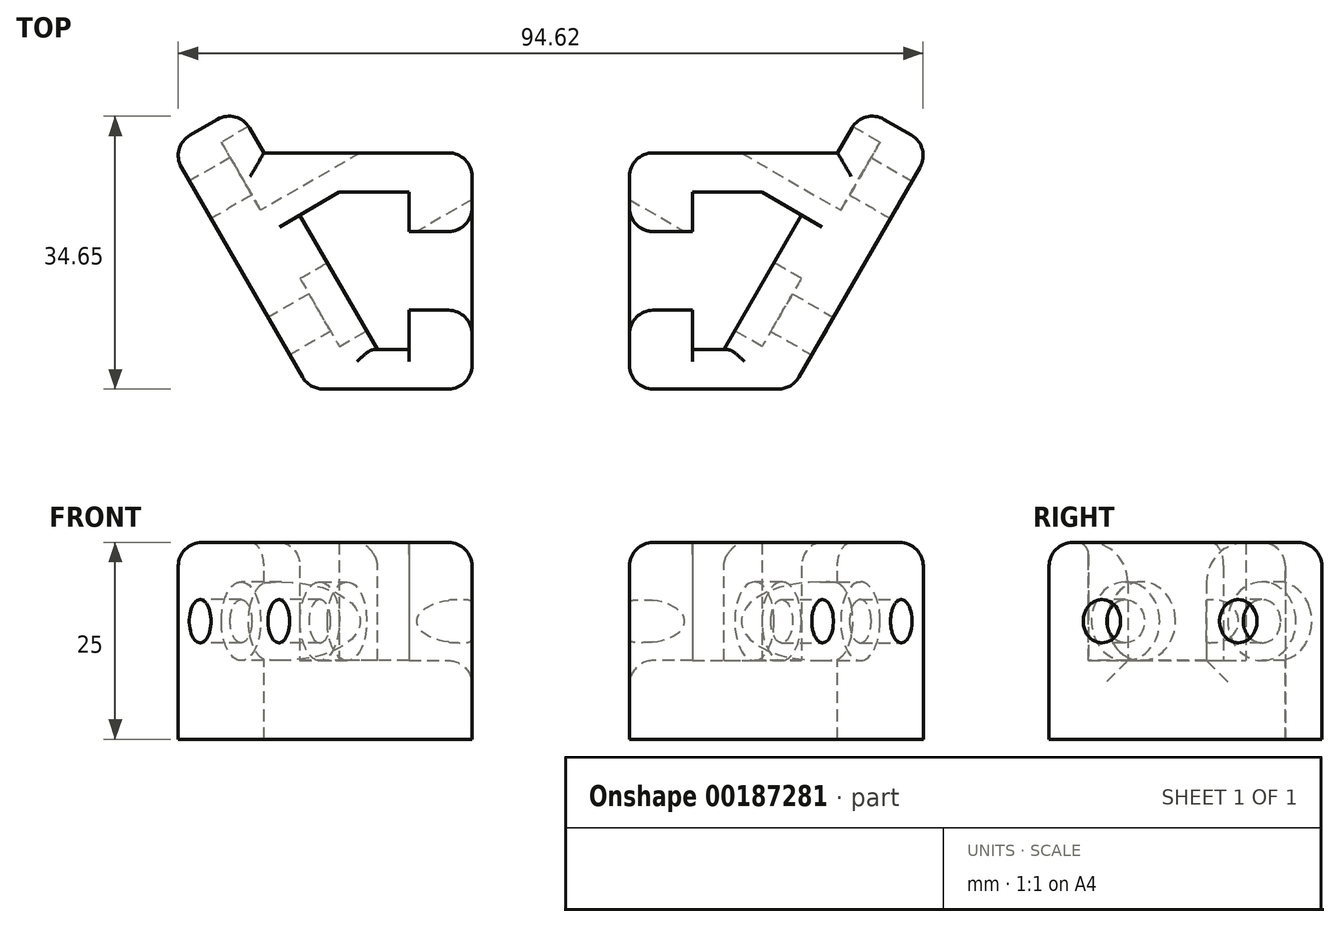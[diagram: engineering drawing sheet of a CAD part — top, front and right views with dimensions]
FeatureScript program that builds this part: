
annotation { "Feature Type Name" : "Feature", "Feature Type Description" : "" }
export const myFeature = defineFeature(function(context is Context, id is Id, definition is map)
    precondition{}
    {
        {
            var Q0;
            Q0=qCreatedBy(makeId("Top.planeOp"),FACE);
            var sketch = newSketch(context, id + "F0", { "sketchPlane" : qUnion([Q0])});
            skLineSegment(sketch, "E0.bottom", {"start": v(-4, 10) * mm, "end": v(4, 10) * mm});
            skLineSegment(sketch, "E0.top", {"start": v(-4, -10) * mm, "end": v(4, -10) * mm});
            skLineSegment(sketch, "E0.left", {"start": v(-4, 10) * mm, "end": v(-4, -10) * mm});
            skLineSegment(sketch, "E0.right", {"start": v(4, 10) * mm, "end": v(4, -10) * mm});
            skPoint(sketch, "E1", {"position": v(0, 10) * mm});
            skPoint(sketch, "E2", {"position": v(4, 0) * mm});
            skLineSegment(sketch, "E3.bottom", {"start": v(-4, 5) * mm, "end": v(4, 5) * mm});
            skLineSegment(sketch, "E3.top", {"start": v(-4, -5) * mm, "end": v(4, -5) * mm});
            skLineSegment(sketch, "E3.left", {"start": v(-4, 5) * mm, "end": v(-4, -5) * mm});
            skLineSegment(sketch, "E3.right", {"start": v(4, 5) * mm, "end": v(4, -5) * mm});
            skPoint(sketch, "E4", {"position": v(-4, 0) * mm});
            skSolve(sketch);
        }
        {
            var Q0;
            {var subQ0=sQuery(id+"F0.wireOp",EDGE,"E0.bottom");Q0=makeQuery(id+"F0.imprint","IMPRINT",FACE,{"disambiguationData":[TD([[makeQuery(id+"F0.imprint","IMPRINT",EDGE,{"derivedFrom":subQ0}),-1.0]])]});}
            var Q1;
            {var subQ0=sQuery(id+"F0.wireOp",EDGE,"E0.top");Q1=makeQuery(id+"F0.imprint","IMPRINT",FACE,{"disambiguationData":[TD([[makeQuery(id+"F0.imprint","IMPRINT",EDGE,{"derivedFrom":subQ0}),1.0]])]});}
            extrude(context, id + "F1", {"entities" : qUnion([Q0, Q1]), "depth" : 25 * mm});
        }
        {
            var Q0;
            Q0=makeQuery(id+"F1.opExtrude","CAP_FACE",FACE,{"disambiguationData":[OSD([sQuery(id+"F0.wireOp",EDGE,"E0.top"),sQuery(id+"F0.wireOp",EDGE,"E0.left"),sQuery(id+"F0.wireOp",EDGE,"E0.right"),sQuery(id+"F0.wireOp",EDGE,"E3.top")])],"isStart":true});
            var sketch = newSketch(context, id + "F2", { "sketchPlane" : qUnion([Q0])});
            skLineSegment(sketch, "E5.bottom", {"start": v(4, -10) * mm, "end": v(-8, -10) * mm});
            skLineSegment(sketch, "E5.top", {"start": v(4, 10) * mm, "end": v(-8, 10) * mm});
            skLineSegment(sketch, "E5.left", {"start": v(4, -10) * mm, "end": v(4, 10) * mm});
            skLineSegment(sketch, "E5.right", {"start": v(-8, -10) * mm, "end": v(-8, 10) * mm});
            skLineSegment(sketch, "E6", {"start": v(-8, 10) * mm, "end": v(-19.55, -10) * mm});
            skLineSegment(sketch, "E7", {"start": v(-8, -10) * mm, "end": v(-19.55, -10) * mm});
            skSolve(sketch);
        }
        {
            var Q0;
            {var subQ4=sQuery(id+"F2.wireOp",EDGE,"E5.bottom");Q0=makeQuery(id+"F2.imprint","IMPRINT",FACE,{"disambiguationData":[TD([[makeQuery(id+"F2.imprint","IMPRINT",EDGE,{"derivedFrom":subQ4}),-1.0]])]});}
            var Q1;
            Q1=makeQuery(id+"F2.imprint","IMPRINT",FACE,{"disambiguationData":[TD([[makeQuery(id+"F2.imprint","IMPRINT",EDGE,{"derivedFrom":sQuery(id+"F2.wireOp",EDGE,"E5.right")}),1.0]])]});
            extrude(context, id + "F3", {"entities" : qUnion([Q0, Q1]), "oppositeDirection" : true, "depth" : 10 * mm});
        }
        {
            var Q0;
            Q0=makeQuery(id+"F3.opExtrude","SWEPT_FACE",FACE,{"disambiguationData":[OSD([sQuery(id+"F2.wireOp",EDGE,"E6")])]});
            var sketch = newSketch(context, id + "F4", { "sketchPlane" : qUnion([Q0])});
            skLineSegment(sketch, "E8.bottom", {"start": v(4.66, 0) * mm, "end": v(-18.43, 0) * mm});
            skLineSegment(sketch, "E8.top", {"start": v(4.66, 25) * mm, "end": v(-18.43, 25) * mm});
            skLineSegment(sketch, "E8.left", {"start": v(4.66, 0) * mm, "end": v(4.66, 25) * mm});
            skLineSegment(sketch, "E8.right", {"start": v(-18.43, 0) * mm, "end": v(-18.43, 25) * mm});
            skSolve(sketch);
        }
        {
            var Q0;
            {var subQ0=sQuery(id+"F4.wireOp",EDGE,"E8.top");Q0=makeQuery(id+"F4.imprint","IMPRINT",FACE,{"disambiguationData":[TD([[makeQuery(id+"F4.imprint","IMPRINT",EDGE,{"derivedFrom":subQ0}),1.0]])]});}
            var Q1;
            {var subQ0=sQuery(id+"F4.wireOp",EDGE,"E8.bottom");Q1=makeQuery(id+"F4.imprint","IMPRINT",FACE,{"disambiguationData":[TD([[makeQuery(id+"F4.imprint","IMPRINT",EDGE,{"derivedFrom":subQ0}),-1.0]])]});}
            extrude(context, id + "F5", {"entities" : qUnion([Q0, Q1]), "operationType" : NewBodyOperationType.ADD, "depth" : 10 * mm});
        }
        {
            var Q0;
            Q0=makeQuery(id+"F1.opExtrude","SWEPT_FACE",FACE,{"disambiguationData":[OSD([sQuery(id+"F0.wireOp",EDGE,"E0.top")])]});
            var sketch = newSketch(context, id + "F6", { "sketchPlane" : qUnion([Q0])});
            skLineSegment(sketch, "E9.bottom", {"start": v(4, 25) * mm, "end": v(-16.66, 25) * mm});
            skLineSegment(sketch, "E9.top", {"start": v(4, 0) * mm, "end": v(-16.66, 0) * mm});
            skLineSegment(sketch, "E9.left", {"start": v(4, 25) * mm, "end": v(4, 0) * mm});
            skLineSegment(sketch, "E9.right", {"start": v(-16.66, 25) * mm, "end": v(-16.66, 0) * mm});
            skSolve(sketch);
        }
        {
            var Q0;
            {var subQ2=sQuery(id+"F6.wireOp",EDGE,"E9.right");Q0=makeQuery(id+"F6.imprint","IMPRINT",FACE,{"disambiguationData":[TD([[makeQuery(id+"F6.imprint","IMPRINT",EDGE,{"derivedFrom":subQ2}),1.0]])]});}
            var Q1;
            {var subQ2=sQuery(id+"F6.wireOp",EDGE,"E9.left");Q1=makeQuery(id+"F6.imprint","IMPRINT",FACE,{"disambiguationData":[TD([[makeQuery(id+"F6.imprint","IMPRINT",EDGE,{"derivedFrom":subQ2}),-1.0]])]});}
            extrude(context, id + "F7", {"entities" : qUnion([Q0, Q1]), "depth" : 2.5 * mm});
        }
        {
            var Q0;
            Q0=makeQuery(id+"F1.opExtrude","SWEPT_FACE",FACE,{"disambiguationData":[OSD([sQuery(id+"F0.wireOp",EDGE,"E0.bottom")])]});
            var sketch = newSketch(context, id + "F8", { "sketchPlane" : qUnion([Q0])});
            skLineSegment(sketch, "E10.bottom", {"start": v(-4, 25) * mm, "end": v(28.2, 25) * mm});
            skLineSegment(sketch, "E10.top", {"start": v(-4, 0) * mm, "end": v(28.2, 0) * mm});
            skLineSegment(sketch, "E10.left", {"start": v(-4, 25) * mm, "end": v(-4, 0) * mm});
            skLineSegment(sketch, "E10.right", {"start": v(28.2, 25) * mm, "end": v(28.2, 0) * mm});
            skSolve(sketch);
        }
        {
            var Q0;
            {var subQ2=sQuery(id+"F8.wireOp",EDGE,"E10.right");Q0=makeQuery(id+"F8.imprint","IMPRINT",FACE,{"disambiguationData":[TD([[makeQuery(id+"F8.imprint","IMPRINT",EDGE,{"derivedFrom":subQ2}),-1.0]])]});}
            var Q1;
            {var subQ2=sQuery(id+"F8.wireOp",EDGE,"E10.left");Q1=makeQuery(id+"F8.imprint","IMPRINT",FACE,{"disambiguationData":[TD([[makeQuery(id+"F8.imprint","IMPRINT",EDGE,{"derivedFrom":subQ2}),1.0]])]});}
            extrude(context, id + "F9", {"entities" : qUnion([Q0, Q1]), "depth" : 5 * mm});
        }
        {
            var Q0;
            Q0=makeQuery(id+"F9.opExtrude","SWEPT_FACE",FACE,{"disambiguationData":[OSD([sQuery(id+"F8.wireOp",EDGE,"E10.bottom")])]});
            var sketch = newSketch(context, id + "F10", { "sketchPlane" : qUnion([Q0])});
            skLineSegment(sketch, "E11", {"start": v(-28.2, 10) * mm, "end": v(-28.2, 5) * mm});
            skLineSegment(sketch, "E12", {"start": v(-28.2, 5) * mm, "end": v(-19.55, 10) * mm});
            skLineSegment(sketch, "E13", {"start": v(-19.55, 10) * mm, "end": v(-28.2, 10) * mm});
            skSolve(sketch);
        }
        {
            var Q0;
            Q0=makeQuery(id+"F10.imprint","IMPRINT",FACE,{"disambiguationData":[TD([[makeQuery(id+"F10.imprint","IMPRINT",EDGE,{"derivedFrom":sQuery(id+"F10.wireOp",EDGE,"E11")}),1.0]])]});
            var Q1;
            Q1=makeQuery(id+"F9.opExtrude","SWEPT_FACE",FACE,{"disambiguationData":[OSD([sQuery(id+"F8.wireOp",EDGE,"E10.top")])]});
            extrude(context, id + "F11", {"entities" : qUnion([Q0]), "endBound" : BoundingType.UP_TO_SURFACE, "oppositeDirection" : true, "endBoundEntityFace" : qUnion([Q1]), "depth" : 25 * mm});
        }
        {
            var Q0;
            Q0=makeQuery(id+"F1.opExtrude","SWEPT_BODY",BODY,{"disambiguationData":[OSD([sQuery(id+"F0.wireOp",EDGE,"E0.bottom"),sQuery(id+"F0.wireOp",EDGE,"E0.left"),sQuery(id+"F0.wireOp",EDGE,"E0.right"),sQuery(id+"F0.wireOp",EDGE,"E3.bottom")])]});
            var Q1;
            Q1=makeQuery(id+"F1.opExtrude","SWEPT_BODY",BODY,{"disambiguationData":[OSD([sQuery(id+"F0.wireOp",EDGE,"E0.top"),sQuery(id+"F0.wireOp",EDGE,"E0.left"),sQuery(id+"F0.wireOp",EDGE,"E0.right"),sQuery(id+"F0.wireOp",EDGE,"E3.top")])]});
            var Q2;
            Q2=makeQuery(id+"F3.opExtrude","SWEPT_BODY",BODY,{"disambiguationData":[OSD([sQuery(id+"F0.wireOp",EDGE,"E0.left"),sQuery(id+"F0.wireOp",EDGE,"E3.top"),sQuery(id+"F2.wireOp",EDGE,"E5.bottom"),sQuery(id+"F2.wireOp",EDGE,"E5.top"),sQuery(id+"F2.wireOp",EDGE,"E5.left"),sQuery(id+"F2.wireOp",EDGE,"E6"),sQuery(id+"F2.wireOp",EDGE,"E7")])]});
            var Q3;
            Q3=makeQuery(id+"F7.opExtrude","SWEPT_BODY",BODY,{"disambiguationData":[OSD([sQuery(id+"F6.wireOp",EDGE,"E9.bottom"),sQuery(id+"F6.wireOp",EDGE,"E9.top"),sQuery(id+"F6.wireOp",EDGE,"E9.left"),sQuery(id+"F6.wireOp",EDGE,"E9.right")])]});
            var Q4;
            Q4=makeQuery(id+"F9.opExtrude","SWEPT_BODY",BODY,{"disambiguationData":[OSD([sQuery(id+"F8.wireOp",EDGE,"E10.bottom"),sQuery(id+"F8.wireOp",EDGE,"E10.top"),sQuery(id+"F8.wireOp",EDGE,"E10.left"),sQuery(id+"F8.wireOp",EDGE,"E10.right")])]});
            var Q5;
            Q5=makeQuery(id+"F11.opExtrude","SWEPT_BODY",BODY,{"disambiguationData":[OSD([sQuery(id+"F10.wireOp",EDGE,"E11"),sQuery(id+"F10.wireOp",EDGE,"E12"),sQuery(id+"F10.wireOp",EDGE,"E13")])]});
            booleanBodies(context, id + "F12", {"operationType" : BooleanOperationType.UNION, "tools" : qUnion([Q0, Q1, Q2, Q3, Q4, Q5])});
        }
        {
            var Q0;
            {var subQ0=sQuery(id+"F0.wireOp",EDGE,"E0.right");var subQ1=sQuery(id+"F0.wireOp",EDGE,"E0.left");Q0=makeQuery(id+"F28.opFillet","SPLIT",FACE,{"disambiguationData":[OD(2.0)],"derivedFrom":makeQuery(id+"F12.opBoolean","MERGE",FACE,{"derivedFrom":[makeQuery(id+"F1.opExtrude","CAP_FACE",FACE,{"disambiguationData":[OSD([sQuery(id+"F0.wireOp",EDGE,"E0.bottom"),subQ1,subQ0,sQuery(id+"F0.wireOp",EDGE,"E3.bottom")])],"isStart":false}),makeQuery(id+"F1.opExtrude","CAP_FACE",FACE,{"disambiguationData":[OSD([sQuery(id+"F0.wireOp",EDGE,"E0.top"),subQ1,subQ0,sQuery(id+"F0.wireOp",EDGE,"E3.top")])],"isStart":false}),makeQuery(id+"F5.opExtrude","SWEPT_FACE",FACE,{"disambiguationData":[OSD([sQuery(id+"F4.wireOp",EDGE,"E8.top")])]}),makeQuery(id+"F7.opExtrude","SWEPT_FACE",FACE,{"disambiguationData":[OSD([sQuery(id+"F6.wireOp",EDGE,"E9.bottom")])]}),makeQuery(id+"F9.opExtrude","SWEPT_FACE",FACE,{"disambiguationData":[OSD([sQuery(id+"F8.wireOp",EDGE,"E10.bottom")])]}),makeQuery(id+"F11.opExtrude","CAP_FACE",FACE,{"disambiguationData":[OSD([sQuery(id+"F10.wireOp",EDGE,"E11"),sQuery(id+"F10.wireOp",EDGE,"E12"),sQuery(id+"F10.wireOp",EDGE,"E13")])],"isStart":true})]})});}
            var sketch = newSketch(context, id + "F13", { "sketchPlane" : qUnion([Q0])});
            skLineSegment(sketch, "E14", {"start": v(-28.2, 5) * mm, "end": v(-32.54, 12.5) * mm});
            skLineSegment(sketch, "E15", {"start": v(-32.54, 12.5) * mm, "end": v(-23.88, 17.5) * mm});
            skLineSegment(sketch, "E16", {"start": v(-23.88, 17.5) * mm, "end": v(-19.55, 10) * mm});
            skLineSegment(sketch, "E17", {"start": v(-28.2, 15) * mm, "end": v(-32.54, 15) * mm});
            skLineSegment(sketch, "E18", {"start": v(-32.54, 15) * mm, "end": v(-32.54, 12.5) * mm});
            skSolve(sketch);
        }
        {
            var Q0;
            {var subQ0=sQuery(id+"F13.wireOp",EDGE,"E14");Q0=makeQuery(id+"F13.imprint","IMPRINT",FACE,{"disambiguationData":[TD([[makeQuery(id+"F13.imprint","IMPRINT",EDGE,{"derivedFrom":subQ0}),-1.0]])]});}
            var Q1;
            {var subQ0=sQuery(id+"F13.wireOp",EDGE,"E17");Q1=makeQuery(id+"F13.imprint","IMPRINT",FACE,{"disambiguationData":[TD([[makeQuery(id+"F13.imprint","IMPRINT",EDGE,{"derivedFrom":subQ0}),1.0]])]});}
            var Q2;
            {var subQ0=sQuery(id+"F8.wireOp",EDGE,"E10.top");var subQ1=sQuery(id+"F0.wireOp",EDGE,"E3.top");var subQ2=sQuery(id+"F0.wireOp",EDGE,"E0.left");var subQ3=sQuery(id+"F0.wireOp",EDGE,"E0.right");Q2=makeQuery(id+"F12.opBoolean","MERGE",FACE,{"derivedFrom":[makeQuery(id+"F1.opExtrude","CAP_FACE",FACE,{"disambiguationData":[OSD([sQuery(id+"F0.wireOp",EDGE,"E0.bottom"),subQ2,subQ3,sQuery(id+"F0.wireOp",EDGE,"E3.bottom")])],"isStart":true}),makeQuery(id+"F1.opExtrude","CAP_FACE",FACE,{"disambiguationData":[OSD([sQuery(id+"F0.wireOp",EDGE,"E0.top"),subQ2,subQ3,subQ1])],"isStart":true}),makeQuery(id+"F5.boolean.opBoolean","MERGE",FACE,{"derivedFrom":[makeQuery(id+"F3.opExtrude","CAP_FACE",FACE,{"disambiguationData":[OSD([subQ2,subQ1,sQuery(id+"F2.wireOp",EDGE,"E5.bottom"),sQuery(id+"F2.wireOp",EDGE,"E5.top"),sQuery(id+"F2.wireOp",EDGE,"E5.left"),sQuery(id+"F2.wireOp",EDGE,"E6"),sQuery(id+"F2.wireOp",EDGE,"E7")])],"isStart":true}),makeQuery(id+"F5.opExtrude","SWEPT_FACE",FACE,{"disambiguationData":[OSD([sQuery(id+"F4.wireOp",EDGE,"E8.bottom")])]})]}),makeQuery(id+"F7.opExtrude","SWEPT_FACE",FACE,{"disambiguationData":[OSD([sQuery(id+"F6.wireOp",EDGE,"E9.top")])]}),makeQuery(id+"F9.opExtrude","SWEPT_FACE",FACE,{"disambiguationData":[OSD([subQ0])]}),makeQuery(id+"F11.opExtrude","CAP_FACE",FACE,{"disambiguationData":[OSD([subQ0])],"isStart":false})]});}
            extrude(context, id + "F14", {"entities" : qUnion([Q0, Q1]), "operationType" : NewBodyOperationType.ADD, "endBound" : BoundingType.UP_TO_SURFACE, "oppositeDirection" : true, "endBoundEntityFace" : qUnion([Q2]), "depth" : 25 * mm});
        }
        {
            var Q0;
            {var subQ0=sQuery(id+"F10.wireOp",EDGE,"E11");var subQ1=sQuery(id+"F8.wireOp",EDGE,"E10.bottom");var subQ2=sQuery(id+"F0.wireOp",EDGE,"E0.right");var subQ3=sQuery(id+"F0.wireOp",EDGE,"E0.left");Q0=makeQuery(id+"F14.boolean.opBoolean","MERGE",FACE,{"derivedFrom":[makeQuery(id+"F12.opBoolean","MERGE",FACE,{"derivedFrom":[makeQuery(id+"F1.opExtrude","CAP_FACE",FACE,{"disambiguationData":[OSD([sQuery(id+"F0.wireOp",EDGE,"E0.bottom"),subQ3,subQ2,sQuery(id+"F0.wireOp",EDGE,"E3.bottom")])],"isStart":false}),makeQuery(id+"F1.opExtrude","CAP_FACE",FACE,{"disambiguationData":[OSD([sQuery(id+"F0.wireOp",EDGE,"E0.top"),subQ3,subQ2,sQuery(id+"F0.wireOp",EDGE,"E3.top")])],"isStart":false}),makeQuery(id+"F5.opExtrude","SWEPT_FACE",FACE,{"disambiguationData":[OSD([sQuery(id+"F4.wireOp",EDGE,"E8.top")])]}),makeQuery(id+"F7.opExtrude","SWEPT_FACE",FACE,{"disambiguationData":[OSD([sQuery(id+"F6.wireOp",EDGE,"E9.bottom")])]}),makeQuery(id+"F9.opExtrude","SWEPT_FACE",FACE,{"disambiguationData":[OSD([subQ1])]}),makeQuery(id+"F11.opExtrude","CAP_FACE",FACE,{"disambiguationData":[OSD([subQ0,sQuery(id+"F10.wireOp",EDGE,"E12"),sQuery(id+"F10.wireOp",EDGE,"E13")])],"isStart":true})]}),makeQuery(id+"F14.opExtrude","CAP_FACE",FACE,{"disambiguationData":[OSD([subQ1,sQuery(id+"F8.wireOp",EDGE,"E10.right"),subQ0,sQuery(id+"F13.wireOp",EDGE,"E14"),sQuery(id+"F13.wireOp",EDGE,"E15")])],"isStart":true})]});}
            var sketch = newSketch(context, id + "F15", { "sketchPlane" : qUnion([Q0])});
            skLineSegment(sketch, "E19", {"start": v(-16.66, -15) * mm, "end": v(4, -15) * mm});
            skLineSegment(sketch, "E20", {"start": v(4, -15) * mm, "end": v(4, -12.5) * mm});
            skLineSegment(sketch, "E21", {"start": v(-16.66, -15) * mm, "end": v(-12.33, -12.5) * mm});
            skLineSegment(sketch, "E22", {"start": v(-12.33, -12.5) * mm, "end": v(4, -12.5) * mm});
            skSolve(sketch);
        }
        {
            var Q0;
            Q0 = qSketchRegion(id + "F15", true);
            var Q1;
            {var subQ0=sQuery(id+"F8.wireOp",EDGE,"E10.top");var subQ1=sQuery(id+"F6.wireOp",EDGE,"E9.top");var subQ2=sQuery(id+"F4.wireOp",EDGE,"E8.bottom");var subQ3=sQuery(id+"F2.wireOp",EDGE,"E7");var subQ4=sQuery(id+"F2.wireOp",EDGE,"E6");var subQ5=sQuery(id+"F2.wireOp",EDGE,"E5.left");var subQ6=sQuery(id+"F2.wireOp",EDGE,"E5.top");var subQ7=sQuery(id+"F2.wireOp",EDGE,"E5.bottom");var subQ8=sQuery(id+"F0.wireOp",EDGE,"E3.top");var subQ9=sQuery(id+"F0.wireOp",EDGE,"E3.bottom");var subQ10=sQuery(id+"F0.wireOp",EDGE,"E0.right");var subQ11=sQuery(id+"F0.wireOp",EDGE,"E0.left");var subQ12=sQuery(id+"F0.wireOp",EDGE,"E0.top");var subQ13=sQuery(id+"F0.wireOp",EDGE,"E0.bottom");Q1=makeQuery(id+"F14.boolean.opBoolean","MERGE",FACE,{"derivedFrom":[makeQuery(id+"F12.opBoolean","MERGE",FACE,{"derivedFrom":[makeQuery(id+"F1.opExtrude","CAP_FACE",FACE,{"disambiguationData":[OSD([subQ13,subQ11,subQ10,subQ9])],"isStart":true}),makeQuery(id+"F1.opExtrude","CAP_FACE",FACE,{"disambiguationData":[OSD([subQ12,subQ11,subQ10,subQ8])],"isStart":true}),makeQuery(id+"F5.boolean.opBoolean","MERGE",FACE,{"derivedFrom":[makeQuery(id+"F3.opExtrude","CAP_FACE",FACE,{"disambiguationData":[OSD([subQ11,subQ8,subQ7,subQ6,subQ5,subQ4,subQ3])],"isStart":true}),makeQuery(id+"F5.opExtrude","SWEPT_FACE",FACE,{"disambiguationData":[OSD([subQ2])]})]}),makeQuery(id+"F7.opExtrude","SWEPT_FACE",FACE,{"disambiguationData":[OSD([subQ1])]}),makeQuery(id+"F9.opExtrude","SWEPT_FACE",FACE,{"disambiguationData":[OSD([subQ0])]}),makeQuery(id+"F11.opExtrude","CAP_FACE",FACE,{"disambiguationData":[OSD([subQ0])],"isStart":false})]}),makeQuery(id+"F14.opExtrude","CAP_FACE",FACE,{"disambiguationData":[OSD([subQ13,subQ12,subQ11,subQ10,subQ9,subQ8,subQ7,subQ6,subQ5,subQ4,subQ3,subQ2,subQ1,subQ0])],"isStart":false})]});}
            extrude(context, id + "F16", {"entities" : qUnion([Q0]), "operationType" : NewBodyOperationType.ADD, "endBound" : BoundingType.UP_TO_SURFACE, "oppositeDirection" : true, "endBoundEntityFace" : qUnion([Q1]), "depth" : 25 * mm});
        }
        {
            var Q0;
            Q0=makeQuery(id+"F14.boolean.opBoolean","MERGE",FACE,{"derivedFrom":[makeQuery(id+"F5.opExtrude","CAP_FACE",FACE,{"disambiguationData":[OSD([sQuery(id+"F4.wireOp",EDGE,"E8.bottom"),sQuery(id+"F4.wireOp",EDGE,"E8.top"),sQuery(id+"F4.wireOp",EDGE,"E8.left"),sQuery(id+"F4.wireOp",EDGE,"E8.right")])],"isStart":false}),makeQuery(id+"F14.opExtrude","SWEPT_FACE",FACE,{"disambiguationData":[OSD([sQuery(id+"F13.wireOp",EDGE,"E14")])]})]});
            var sketch = newSketch(context, id + "F17", { "sketchPlane" : qUnion([Q0])});
            skCircle(sketch, "E23", {"center": v(-23.09, 15) * mm, "radius": 2.75 * mm});
            skCircle(sketch, "E24", {"center": v(-3.09, 15) * mm, "radius": 2.75 * mm});
            skLineSegment(sketch, "E25", {"start": v(-23.09, 15) * mm, "end": v(-3.09, 15) * mm});
            skPoint(sketch, "E26", {"position": v(-13.09, 15) * mm});
            skLineSegment(sketch, "E27.bottom", {"start": v(-30.84, 25) * mm, "end": v(4.66, 25) * mm});
            skLineSegment(sketch, "E27.top", {"start": v(-30.84, 0) * mm, "end": v(4.66, 0) * mm});
            skLineSegment(sketch, "E27.left", {"start": v(-30.84, 25) * mm, "end": v(-30.84, 0) * mm});
            skLineSegment(sketch, "E27.right", {"start": v(4.66, 25) * mm, "end": v(4.66, 0) * mm});
            skPoint(sketch, "E28", {"position": v(-11.22, 25) * mm});
            skSolve(sketch);
        }
        {
            var Q0;
            Q0=makeQuery(id+"F17.imprint","IMPRINT",FACE,{"disambiguationData":[TD([[makeQuery(id+"F17.imprint","IMPRINT",EDGE,{"derivedFrom":sQuery(id+"F17.wireOp",EDGE,"E24")}),-1.0]])]});
            var Q1;
            {var subQ0=sQuery(id+"F17.wireOp",EDGE,"E27.left");Q1=makeQuery(id+"F17.imprint","IMPRINT",FACE,{"disambiguationData":[TD([[makeQuery(id+"F17.imprint","IMPRINT",EDGE,{"derivedFrom":subQ0}),1.0]])]});}
            extrude(context, id + "F18", {"entities" : qUnion([Q0, Q1]), "operationType" : NewBodyOperationType.ADD, "oppositeDirection" : true, "depth" : 10 * mm});
        }
        {
            var Q0;
            Q0=makeQuery(id+"F18.boolean.opBoolean","MERGE",FACE,{"derivedFrom":[makeQuery(id+"F14.boolean.opBoolean","MERGE",FACE,{"derivedFrom":[makeQuery(id+"F5.opExtrude","CAP_FACE",FACE,{"disambiguationData":[OSD([sQuery(id+"F4.wireOp",EDGE,"E8.bottom"),sQuery(id+"F4.wireOp",EDGE,"E8.top"),sQuery(id+"F4.wireOp",EDGE,"E8.left"),sQuery(id+"F4.wireOp",EDGE,"E8.right")])],"isStart":false}),makeQuery(id+"F14.opExtrude","SWEPT_FACE",FACE,{"disambiguationData":[OSD([sQuery(id+"F13.wireOp",EDGE,"E14")])]})]}),makeQuery(id+"F18.opExtrude","CAP_FACE",FACE,{"disambiguationData":[OSD([sQuery(id+"F17.wireOp",EDGE,"E23"),sQuery(id+"F17.wireOp",EDGE,"E24"),sQuery(id+"F17.wireOp",EDGE,"E27.bottom"),sQuery(id+"F17.wireOp",EDGE,"E27.top"),sQuery(id+"F17.wireOp",EDGE,"E27.left"),sQuery(id+"F17.wireOp",EDGE,"E27.right")])],"isStart":true})]});
            var sketch = newSketch(context, id + "F19", { "sketchPlane" : qUnion([Q0])});
            skCircle(sketch, "E29", {"center": v(-3.09, 15) * mm, "radius": 2.75 * mm});
            skCircle(sketch, "E30", {"center": v(-23.09, 15) * mm, "radius": 2.75 * mm});
            skSolve(sketch);
        }
        {
            var Q0;
            Q0=makeQuery(id+"F19.imprint","IMPRINT",FACE,{"disambiguationData":[TD([[makeQuery(id+"F19.imprint","IMPRINT",EDGE,{"derivedFrom":sQuery(id+"F19.wireOp",EDGE,"E29")}),1.0]])]});
            var Q1;
            {var subQ1=makeQuery(id+"F14.opExtrude","SWEPT_EDGE",EDGE,{"disambiguationData":[OSD([sQuery(id+"F13.wireOp",EDGE,"E14"),sQuery(id+"F13.wireOp",EDGE,"E15"),sQuery(id+"F13.wireOp",EDGE,"E18")])]});Q1=makeQuery(id+"F19.imprint","IMPRINT",FACE,{"disambiguationData":[TD([[makeQuery(id+"F19.imprint","IMPRINT",EDGE,{"derivedFrom":subQ1}),-1.0]])]});}
            var Q2;
            {var subQ1=makeQuery(id+"F14.opExtrude","SWEPT_EDGE",EDGE,{"disambiguationData":[OSD([sQuery(id+"F13.wireOp",EDGE,"E14"),sQuery(id+"F13.wireOp",EDGE,"E15"),sQuery(id+"F13.wireOp",EDGE,"E18")])]});Q2=makeQuery(id+"F19.imprint","IMPRINT",FACE,{"disambiguationData":[TD([[makeQuery(id+"F19.imprint","IMPRINT",EDGE,{"derivedFrom":subQ1}),1.0]])]});}
            var Q3;
            Q3=makeQuery(id+"F19.imprint","IMPRINT",FACE,{"disambiguationData":[TD([[makeQuery(id+"F19.imprint","IMPRINT",EDGE,{"derivedFrom":sQuery(id+"F19.wireOp",EDGE,"E30")}),1.0]])]});
            extrude(context, id + "F20", {"entities" : qUnion([Q0, Q1, Q2, Q3]), "operationType" : NewBodyOperationType.REMOVE, "endBound" : BoundingType.THROUGH_ALL, "oppositeDirection" : true, "depth" : 25 * mm});
        }
        {
            var Q0;
            Q0=makeQuery(id+"F3.opExtrude","CAP_FACE",FACE,{"disambiguationData":[OSD([sQuery(id+"F0.wireOp",EDGE,"E0.left"),sQuery(id+"F0.wireOp",EDGE,"E3.top"),sQuery(id+"F2.wireOp",EDGE,"E5.bottom"),sQuery(id+"F2.wireOp",EDGE,"E5.top"),sQuery(id+"F2.wireOp",EDGE,"E5.left"),sQuery(id+"F2.wireOp",EDGE,"E6"),sQuery(id+"F2.wireOp",EDGE,"E7")])],"isStart":false});
            var sketch = newSketch(context, id + "F21", { "sketchPlane" : qUnion([Q0])});
            skLineSegment(sketch, "E31", {"start": v(-17.87, 7.1) * mm, "end": v(-12.86, 10) * mm});
            skSolve(sketch);
        }
        {
            var Q0;
            {var subQ0=sQuery(id+"F21.wireOp",EDGE,"E31");Q0=makeQuery(id+"F21.imprint","IMPRINT",FACE,{"disambiguationData":[TD([[makeQuery(id+"F21.imprint","IMPRINT",EDGE,{"derivedFrom":subQ0}),1.0]])]});}
            var Q1;
            {var subQ0=sQuery(id+"F10.wireOp",EDGE,"E11");var subQ1=sQuery(id+"F8.wireOp",EDGE,"E10.bottom");var subQ2=sQuery(id+"F0.wireOp",EDGE,"E0.right");var subQ3=sQuery(id+"F0.wireOp",EDGE,"E0.left");Q1=makeQuery(id+"F16.boolean.opBoolean","MERGE",FACE,{"derivedFrom":[makeQuery(id+"F14.boolean.opBoolean","MERGE",FACE,{"derivedFrom":[makeQuery(id+"F12.opBoolean","MERGE",FACE,{"derivedFrom":[makeQuery(id+"F1.opExtrude","CAP_FACE",FACE,{"disambiguationData":[OSD([sQuery(id+"F0.wireOp",EDGE,"E0.bottom"),subQ3,subQ2,sQuery(id+"F0.wireOp",EDGE,"E3.bottom")])],"isStart":false}),makeQuery(id+"F1.opExtrude","CAP_FACE",FACE,{"disambiguationData":[OSD([sQuery(id+"F0.wireOp",EDGE,"E0.top"),subQ3,subQ2,sQuery(id+"F0.wireOp",EDGE,"E3.top")])],"isStart":false}),makeQuery(id+"F5.opExtrude","SWEPT_FACE",FACE,{"disambiguationData":[OSD([sQuery(id+"F4.wireOp",EDGE,"E8.top")])]}),makeQuery(id+"F7.opExtrude","SWEPT_FACE",FACE,{"disambiguationData":[OSD([sQuery(id+"F6.wireOp",EDGE,"E9.bottom")])]}),makeQuery(id+"F9.opExtrude","SWEPT_FACE",FACE,{"disambiguationData":[OSD([subQ1])]}),makeQuery(id+"F11.opExtrude","CAP_FACE",FACE,{"disambiguationData":[OSD([subQ0,sQuery(id+"F10.wireOp",EDGE,"E12"),sQuery(id+"F10.wireOp",EDGE,"E13")])],"isStart":true})]}),makeQuery(id+"F14.opExtrude","CAP_FACE",FACE,{"disambiguationData":[OSD([subQ1,sQuery(id+"F8.wireOp",EDGE,"E10.right"),subQ0,sQuery(id+"F13.wireOp",EDGE,"E14"),sQuery(id+"F13.wireOp",EDGE,"E17"),sQuery(id+"F13.wireOp",EDGE,"E18")])],"isStart":true})]}),makeQuery(id+"F16.opExtrude","CAP_FACE",FACE,{"disambiguationData":[OSD([sQuery(id+"F15.wireOp",EDGE,"E19"),sQuery(id+"F15.wireOp",EDGE,"E20"),sQuery(id+"F15.wireOp",EDGE,"E21"),sQuery(id+"F15.wireOp",EDGE,"E22")])],"isStart":true})]});}
            extrude(context, id + "F22", {"entities" : qUnion([Q0]), "operationType" : NewBodyOperationType.ADD, "endBound" : BoundingType.UP_TO_SURFACE, "endBoundEntityFace" : qUnion([Q1]), "depth" : 25 * mm});
        }
        {
            var Q0;
            Q0=makeQuery(id+"F18.opExtrude","CAP_FACE",FACE,{"disambiguationData":[OSD([sQuery(id+"F17.wireOp",EDGE,"E23"),sQuery(id+"F17.wireOp",EDGE,"E24"),sQuery(id+"F17.wireOp",EDGE,"E27.bottom"),sQuery(id+"F17.wireOp",EDGE,"E27.top"),sQuery(id+"F17.wireOp",EDGE,"E27.left"),sQuery(id+"F17.wireOp",EDGE,"E27.right")])],"isStart":false});
            var sketch = newSketch(context, id + "F23", { "sketchPlane" : qUnion([Q0])});
            skCircle(sketch, "E32", {"center": v(23.09, 15) * mm, "radius": 5 * mm});
            skSolve(sketch);
        }
        {
            var Q0;
            {var subQ1=sQuery(id+"F17.wireOp",EDGE,"E23");Q0=makeQuery(id+"F23.imprint","IMPRINT",FACE,{"disambiguationData":[TD([[makeQuery(id+"F23.imprint","IMPRINT",EDGE,{"derivedFrom":makeQuery(id+"F18.opExtrude","CAP_EDGE",EDGE,{"disambiguationData":[OSD([subQ1])],"isStart":false})}),1.0]])]});}
            var Q1;
            {var subQ0=sQuery(id+"F23.wireOp",EDGE,"E32");var subQ1=makeQuery(id+"F18.boolean.opBoolean","INTERSECT",EDGE,{"derivedFrom":[makeQuery(id+"F14.boolean.opBoolean","MERGE",FACE,{"derivedFrom":[makeQuery(id+"F9.opExtrude","CAP_FACE",FACE,{"disambiguationData":[OSD([sQuery(id+"F8.wireOp",EDGE,"E10.bottom"),sQuery(id+"F8.wireOp",EDGE,"E10.top"),sQuery(id+"F8.wireOp",EDGE,"E10.left"),sQuery(id+"F8.wireOp",EDGE,"E10.right")])],"isStart":false}),makeQuery(id+"F14.opExtrude","SWEPT_FACE",FACE,{"disambiguationData":[OSD([sQuery(id+"F13.wireOp",EDGE,"E17")])]})]}),makeQuery(id+"F18.opExtrude","CAP_FACE",FACE,{"disambiguationData":[OSD([sQuery(id+"F17.wireOp",EDGE,"E23"),sQuery(id+"F17.wireOp",EDGE,"E24"),sQuery(id+"F17.wireOp",EDGE,"E27.bottom"),sQuery(id+"F17.wireOp",EDGE,"E27.top"),sQuery(id+"F17.wireOp",EDGE,"E27.left"),sQuery(id+"F17.wireOp",EDGE,"E27.right")])],"isStart":false})]});var subQ2=makeQuery(id+"F23.imprint","INTERSECT",VERTEX,{"disambiguationData":[OD(0.0)],"derivedFrom":[subQ1,subQ0]});Q1=makeQuery(id+"F23.imprint","IMPRINT",FACE,{"disambiguationData":[TD([[makeQuery(id+"F23.imprint","IMPRINT",EDGE,{"disambiguationData":[TD([[subQ2,-1.0]])],"derivedFrom":subQ0}),1.0]])]});}
            extrude(context, id + "F24", {"entities" : qUnion([Q0, Q1]), "operationType" : NewBodyOperationType.REMOVE, "depth" : 25 * mm});
        }
        {
            var Q0;
            Q0=makeQuery(id+"F5.opExtrude","CAP_FACE",FACE,{"disambiguationData":[OSD([sQuery(id+"F4.wireOp",EDGE,"E8.bottom"),sQuery(id+"F4.wireOp",EDGE,"E8.top"),sQuery(id+"F4.wireOp",EDGE,"E8.left"),sQuery(id+"F4.wireOp",EDGE,"E8.right")])],"isStart":true});
            var sketch = newSketch(context, id + "F25", { "sketchPlane" : qUnion([Q0])});
            skCircle(sketch, "E33", {"center": v(3.09, 15) * mm, "radius": 5 * mm});
            skCircle(sketch, "E34", {"center": v(23.09, 15) * mm, "radius": 5 * mm});
            skSolve(sketch);
        }
        {
            var Q0;
            Q0=makeQuery(id+"F25.imprint","IMPRINT",FACE,{"disambiguationData":[TD([[makeQuery(id+"F25.imprint","IMPRINT",EDGE,{"derivedFrom":sQuery(id+"F25.wireOp",EDGE,"E33")}),1.0]])]});
            var Q1;
            Q1=makeQuery(id+"F25.imprint","IMPRINT",FACE,{"disambiguationData":[TD([[makeQuery(id+"F25.imprint","IMPRINT",EDGE,{"derivedFrom":sQuery(id+"F25.wireOp",EDGE,"E34")}),1.0]])]});
            extrude(context, id + "F26", {"entities" : qUnion([Q0, Q1]), "operationType" : NewBodyOperationType.REMOVE, "oppositeDirection" : true, "depth" : 4 * mm});
        }
        {
            var Q0;
            Q0=makeQuery(id+"F1.opExtrude","CAP_EDGE",EDGE,{"disambiguationData":[OSD([sQuery(id+"F0.wireOp",EDGE,"E3.top")])],"isStart":false});
            var Q1;
            Q1=makeQuery(id+"F1.opExtrude","CAP_EDGE",EDGE,{"disambiguationData":[OSD([sQuery(id+"F0.wireOp",EDGE,"E3.bottom")])],"isStart":false});
            fillet(context, id + "F27", {"entities" : qUnion([Q0, Q1]), "radius" : 5 * mm, "tangentPropagation" : true, "allowEdgeOverflow" : false});
        }
        {
            var Q0;
            Q0=makeQuery(id+"F3.opExtrude","CAP_EDGE",EDGE,{"disambiguationData":[OSD([sQuery(id+"F2.wireOp",EDGE,"E5.left")])],"isStart":false});
            var Q1;
            Q1=makeQuery(id+"F1.opExtrude","SWEPT_EDGE",EDGE,{"disambiguationData":[OSD([sQuery(id+"F0.wireOp",EDGE,"E0.right"),sQuery(id+"F0.wireOp",EDGE,"E3.top"),sQuery(id+"F0.wireOp",EDGE,"E3.right")])]});
            var Q2;
            {var subQ0=sQuery(id+"F2.wireOp",EDGE,"E5.left");var subQ1=sQuery(id+"F0.wireOp",EDGE,"E3.top");var subQ2=sQuery(id+"F0.wireOp",EDGE,"E3.bottom");var subQ3=sQuery(id+"F0.wireOp",EDGE,"E0.right");var subQ4=sQuery(id+"F0.wireOp",EDGE,"E3.right");Q2=makeQuery(id+"F20.boolean.opBoolean","SPLIT",EDGE,{"disambiguationData":[TD([makeQuery(id+"F3.opExtrude","CAP_FACE",FACE,{"disambiguationData":[OSD([sQuery(id+"F0.wireOp",EDGE,"E0.left"),subQ1,sQuery(id+"F2.wireOp",EDGE,"E5.bottom"),sQuery(id+"F2.wireOp",EDGE,"E5.top"),subQ0,sQuery(id+"F2.wireOp",EDGE,"E6"),sQuery(id+"F2.wireOp",EDGE,"E7")])],"isStart":false})])],"derivedFrom":makeQuery(id+"F1.opExtrude","SWEPT_EDGE",EDGE,{"disambiguationData":[OSD([subQ3,subQ2,subQ4])]})});}
            var Q3;
            {var subQ2=sQuery(id+"F0.wireOp",EDGE,"E3.bottom");var subQ3=sQuery(id+"F0.wireOp",EDGE,"E0.right");var subQ6=sQuery(id+"F0.wireOp",EDGE,"E3.right");Q3=makeQuery(id+"F20.boolean.opBoolean","SPLIT",EDGE,{"disambiguationData":[TD([makeQuery(id+"F5.opExtrude","SWEPT_FACE",FACE,{"disambiguationData":[OSD([sQuery(id+"F4.wireOp",EDGE,"E8.top")])]})])],"derivedFrom":makeQuery(id+"F1.opExtrude","SWEPT_EDGE",EDGE,{"disambiguationData":[OSD([subQ3,subQ2,subQ6])]})});}
            var Q4;
            Q4=makeQuery(id+"F16.opExtrude","SWEPT_EDGE",EDGE,{"disambiguationData":[OSD([sQuery(id+"F15.wireOp",EDGE,"E19"),sQuery(id+"F15.wireOp",EDGE,"E20")])]});
            var Q5;
            Q5=makeQuery(id+"F9.opExtrude","CAP_EDGE",EDGE,{"disambiguationData":[OSD([sQuery(id+"F8.wireOp",EDGE,"E10.left")])],"isStart":false});
            var Q6;
            Q6=makeQuery(id+"F14.boolean.opBoolean","MERGE",EDGE,{"derivedFrom":[makeQuery(id+"F9.opExtrude","CAP_EDGE",EDGE,{"disambiguationData":[OSD([sQuery(id+"F8.wireOp",EDGE,"E10.bottom")])],"isStart":false}),makeQuery(id+"F14.opExtrude","CAP_EDGE",EDGE,{"disambiguationData":[OSD([sQuery(id+"F13.wireOp",EDGE,"E17")])],"isStart":true})]});
            var Q7;
            Q7=makeQuery(id+"F16.opExtrude","CAP_EDGE",EDGE,{"disambiguationData":[OSD([sQuery(id+"F15.wireOp",EDGE,"E19")])],"isStart":true});
            var Q8;
            Q8=makeQuery(id+"F18.opExtrude","CAP_EDGE",EDGE,{"disambiguationData":[OSD([sQuery(id+"F17.wireOp",EDGE,"E27.left")])],"isStart":false});
            var Q9;
            Q9=makeQuery(id+"F18.opExtrude","CAP_EDGE",EDGE,{"disambiguationData":[OSD([sQuery(id+"F17.wireOp",EDGE,"E27.left")])],"isStart":true});
            var Q10;
            Q10=makeQuery(id+"F16.boolean.opBoolean","MERGE",EDGE,{"derivedFrom":[makeQuery(id+"F5.opExtrude","CAP_EDGE",EDGE,{"disambiguationData":[OSD([sQuery(id+"F4.wireOp",EDGE,"E8.left")])],"isStart":false}),makeQuery(id+"F16.opExtrude","SWEPT_EDGE",EDGE,{"disambiguationData":[OSD([sQuery(id+"F4.wireOp",EDGE,"E8.top"),sQuery(id+"F13.wireOp",EDGE,"E14"),sQuery(id+"F15.wireOp",EDGE,"E19"),sQuery(id+"F15.wireOp",EDGE,"E21")])]})]});
            var Q11;
            Q11=makeQuery(id+"F5.opExtrude","CAP_EDGE",EDGE,{"disambiguationData":[OSD([sQuery(id+"F4.wireOp",EDGE,"E8.top")])],"isStart":true});
            var Q12;
            Q12=makeQuery(id+"F18.boolean.opBoolean","MERGE",EDGE,{"derivedFrom":[makeQuery(id+"F14.boolean.opBoolean","MERGE",EDGE,{"derivedFrom":[makeQuery(id+"F5.opExtrude","CAP_EDGE",EDGE,{"disambiguationData":[OSD([sQuery(id+"F4.wireOp",EDGE,"E8.top")])],"isStart":false}),makeQuery(id+"F14.opExtrude","CAP_EDGE",EDGE,{"disambiguationData":[OSD([sQuery(id+"F13.wireOp",EDGE,"E14")])],"isStart":true})]}),makeQuery(id+"F18.opExtrude","CAP_EDGE",EDGE,{"disambiguationData":[OSD([sQuery(id+"F17.wireOp",EDGE,"E27.bottom")])],"isStart":true})]});
            var Q13;
            Q13=makeQuery(id+"F18.opExtrude","CAP_EDGE",EDGE,{"disambiguationData":[OSD([sQuery(id+"F17.wireOp",EDGE,"E27.bottom")])],"isStart":false});
            var Q14;
            Q14=makeQuery(id+"F18.opExtrude","SWEPT_EDGE",EDGE,{"disambiguationData":[OSD([sQuery(id+"F17.wireOp",EDGE,"E27.bottom"),sQuery(id+"F17.wireOp",EDGE,"E27.left")])]});
            fillet(context, id + "F28", {"entities" : qUnion([Q0, Q1, Q2, Q3, Q4, Q5, Q6, Q7, Q8, Q9, Q10, Q11, Q12, Q13, Q14]), "radius" : 3 * mm, "tangentPropagation" : true, "allowEdgeOverflow" : false});
        }
        {
            var Q0;
            Q0=makeQuery(id+"F5.boolean.opBoolean","SPLIT",EDGE,{"derivedFrom":makeQuery(id+"F5.opExtrude","CAP_EDGE",EDGE,{"disambiguationData":[OSD([sQuery(id+"F4.wireOp",EDGE,"E8.left")])],"isStart":true})});
            var Q1;
            Q1=makeQuery(id+"F22.opExtrude","SWEPT_EDGE",EDGE,{"disambiguationData":[OSD([sQuery(id+"F2.wireOp",EDGE,"E6"),sQuery(id+"F21.wireOp",EDGE,"E31")])]});
            var Q2;
            Q2=makeQuery(id+"F22.opExtrude","SWEPT_EDGE",EDGE,{"disambiguationData":[OSD([sQuery(id+"F2.wireOp",EDGE,"E5.bottom"),sQuery(id+"F2.wireOp",EDGE,"E7"),sQuery(id+"F21.wireOp",EDGE,"E31")])]});
            var Q3;
            {var subQ0=sQuery(id+"F10.wireOp",EDGE,"E11");var subQ1=sQuery(id+"F8.wireOp",EDGE,"E10.bottom");var subQ2=sQuery(id+"F0.wireOp",EDGE,"E0.right");var subQ3=sQuery(id+"F0.wireOp",EDGE,"E0.left");Q3=makeQuery(id+"F22.opExtrude","TWEAK_EDGE",EDGE,{"derivedFrom":[makeQuery(id+"F16.boolean.opBoolean","MERGE",FACE,{"derivedFrom":[makeQuery(id+"F14.boolean.opBoolean","MERGE",FACE,{"derivedFrom":[makeQuery(id+"F12.opBoolean","MERGE",FACE,{"derivedFrom":[makeQuery(id+"F1.opExtrude","CAP_FACE",FACE,{"disambiguationData":[OSD([sQuery(id+"F0.wireOp",EDGE,"E0.bottom"),subQ3,subQ2,sQuery(id+"F0.wireOp",EDGE,"E3.bottom")])],"isStart":false}),makeQuery(id+"F1.opExtrude","CAP_FACE",FACE,{"disambiguationData":[OSD([sQuery(id+"F0.wireOp",EDGE,"E0.top"),subQ3,subQ2,sQuery(id+"F0.wireOp",EDGE,"E3.top")])],"isStart":false}),makeQuery(id+"F5.opExtrude","SWEPT_FACE",FACE,{"disambiguationData":[OSD([sQuery(id+"F4.wireOp",EDGE,"E8.top")])]}),makeQuery(id+"F7.opExtrude","SWEPT_FACE",FACE,{"disambiguationData":[OSD([sQuery(id+"F6.wireOp",EDGE,"E9.bottom")])]}),makeQuery(id+"F9.opExtrude","SWEPT_FACE",FACE,{"disambiguationData":[OSD([subQ1])]}),makeQuery(id+"F11.opExtrude","CAP_FACE",FACE,{"disambiguationData":[OSD([subQ0,sQuery(id+"F10.wireOp",EDGE,"E12"),sQuery(id+"F10.wireOp",EDGE,"E13")])],"isStart":true})]}),makeQuery(id+"F14.opExtrude","CAP_FACE",FACE,{"disambiguationData":[OSD([subQ1,sQuery(id+"F8.wireOp",EDGE,"E10.right"),subQ0,sQuery(id+"F13.wireOp",EDGE,"E14"),sQuery(id+"F13.wireOp",EDGE,"E17"),sQuery(id+"F13.wireOp",EDGE,"E18")])],"isStart":true})]}),makeQuery(id+"F16.opExtrude","CAP_FACE",FACE,{"disambiguationData":[OSD([sQuery(id+"F15.wireOp",EDGE,"E19"),sQuery(id+"F15.wireOp",EDGE,"E20"),sQuery(id+"F15.wireOp",EDGE,"E21"),sQuery(id+"F15.wireOp",EDGE,"E22")])],"isStart":true})]}),makeQuery(id+"F21.imprint","IMPRINT",EDGE,{"derivedFrom":sQuery(id+"F21.wireOp",EDGE,"E31")})]});}
            var Q4;
            Q4=makeQuery(id+"F7.opExtrude","CAP_EDGE",EDGE,{"disambiguationData":[OSD([sQuery(id+"F6.wireOp",EDGE,"E9.bottom")])],"isStart":true});
            fillet(context, id + "F29", {"entities" : qUnion([Q0, Q1, Q2, Q3, Q4]), "radius" : 1.5 * mm, "tangentPropagation" : true, "allowEdgeOverflow" : false});
        }
        {
            var Q0;
            {var subQ0=sQuery(id+"F0.wireOp",EDGE,"E0.right");Q0=makeQuery(id+"F28.opFillet","SPLIT",FACE,{"disambiguationData":[OD(1.0)],"derivedFrom":makeQuery(id+"F16.boolean.opBoolean","MERGE",FACE,{"derivedFrom":[makeQuery(id+"F12.opBoolean","MERGE",FACE,{"derivedFrom":[makeQuery(id+"F1.opExtrude","SWEPT_FACE",FACE,{"disambiguationData":[OSD([subQ0]),TDD([makeQuery(id+"F0.imprint","IMPRINT",EDGE,{"disambiguationData":[TD([[makeQuery(id+"F0.imprint","INTERSECT",VERTEX,{"derivedFrom":[sQuery(id+"F0.wireOp",EDGE,"E0.bottom"),subQ0]}),-1.0]])],"derivedFrom":subQ0})])]}),makeQuery(id+"F1.opExtrude","SWEPT_FACE",FACE,{"disambiguationData":[OSD([subQ0]),TDD([makeQuery(id+"F0.imprint","IMPRINT",EDGE,{"disambiguationData":[TD([[makeQuery(id+"F0.imprint","INTERSECT",VERTEX,{"derivedFrom":[sQuery(id+"F0.wireOp",EDGE,"E0.top"),subQ0]}),1.0]])],"derivedFrom":subQ0})])]}),makeQuery(id+"F3.opExtrude","SWEPT_FACE",FACE,{"disambiguationData":[OSD([sQuery(id+"F2.wireOp",EDGE,"E5.left")])]}),makeQuery(id+"F7.opExtrude","SWEPT_FACE",FACE,{"disambiguationData":[OSD([sQuery(id+"F6.wireOp",EDGE,"E9.left")])]}),makeQuery(id+"F9.opExtrude","SWEPT_FACE",FACE,{"disambiguationData":[OSD([sQuery(id+"F8.wireOp",EDGE,"E10.left")])]})]}),makeQuery(id+"F16.opExtrude","SWEPT_FACE",FACE,{"disambiguationData":[OSD([sQuery(id+"F15.wireOp",EDGE,"E20")])]})]})});}
            cPlane(context, id + "F30", {"entities" : qUnion([Q0]), "cplaneType" : CPlaneType.OFFSET, "offset" : 10 * mm, "width" : 150 * mm, "height" : 150 * mm});
        }
        {
            var Q0;
            Q0=makeQuery(id+"F1.opExtrude","SWEPT_BODY",BODY,{"disambiguationData":[OSD([sQuery(id+"F0.wireOp",EDGE,"E0.bottom"),sQuery(id+"F0.wireOp",EDGE,"E0.left"),sQuery(id+"F0.wireOp",EDGE,"E0.right"),sQuery(id+"F0.wireOp",EDGE,"E3.bottom")])]});
            var Q1;
            Q1=qCreatedBy(id+"F30.planeOp",FACE);
            mirror(context, id + "F31", {"entities" : qUnion([Q0]), "mirrorPlane" : qUnion([Q1])});
        }
    });
